# Revit family: Flowerpot table lamp VP4
name_source: partatom
category: Furniture
revit_build: Autodesk Revit 2017 (Build: 20171027_0315(x64)
units: mm (PartAtom-declared; Revit-internal decimal feet)

## family parameters
Always vertical = Yes
Cut with Voids When Loaded = No
OmniClass Number = 23.40.20.00
OmniClass Title = General Furniture and Specialties
Room Calculation Point = No
Shared = No
Work Plane-Based = No

## types (1)
- Flowerpot table lamp VP4
    Cord = &tradition Plastic Black Matt
    Description = The Flowerpot lamp became synonymous with the Flower Power movement from the late 60s. Reflecting a break from convention to embrace a more open, modern mentality that promoted peace and harmony. Such was the mindset of its designer, Verner Panton. One of the most forward-thinking talents of his time. The Flowerpot series consitsts of several different models, including three pendants and two table lamps - all in a wide range of colours.
    Design = Verner Panton
    Design Year = 1968
    Diameter = 23cm/9.1in
    Height = 36cm/14.2in
    Lamp Base = &tradition Powder Coated Aluminium black
    Lamp Shade bearing = &tradition Plastic White Matt
    Lamp details = &tradition Plastic Black Matt
    Lamp feet = &tradition Powder Coated Aluminium black
    Lamp shade = &tradition Powder Coated Aluminium black
    Lamp shade inside = &tradition Powder Coated Aluminium white
    Lamp top = &tradition Chrome
    Manufacturer = &tradition
    Model = Flowerpot VP4
    Packaging Dimensions = H: 40cm / 15.7in, W: 25.5cm / 10in, D: 25.5cm / 10in
    Socket = &tradition White porcelain
    URL = https://www.andtradition.com
    Variations = Matt White
    Weight = 1.23 kg

## geometry (parser evidence)
native form markers: Sweep x2
no freeform markers — native parametric forms only
